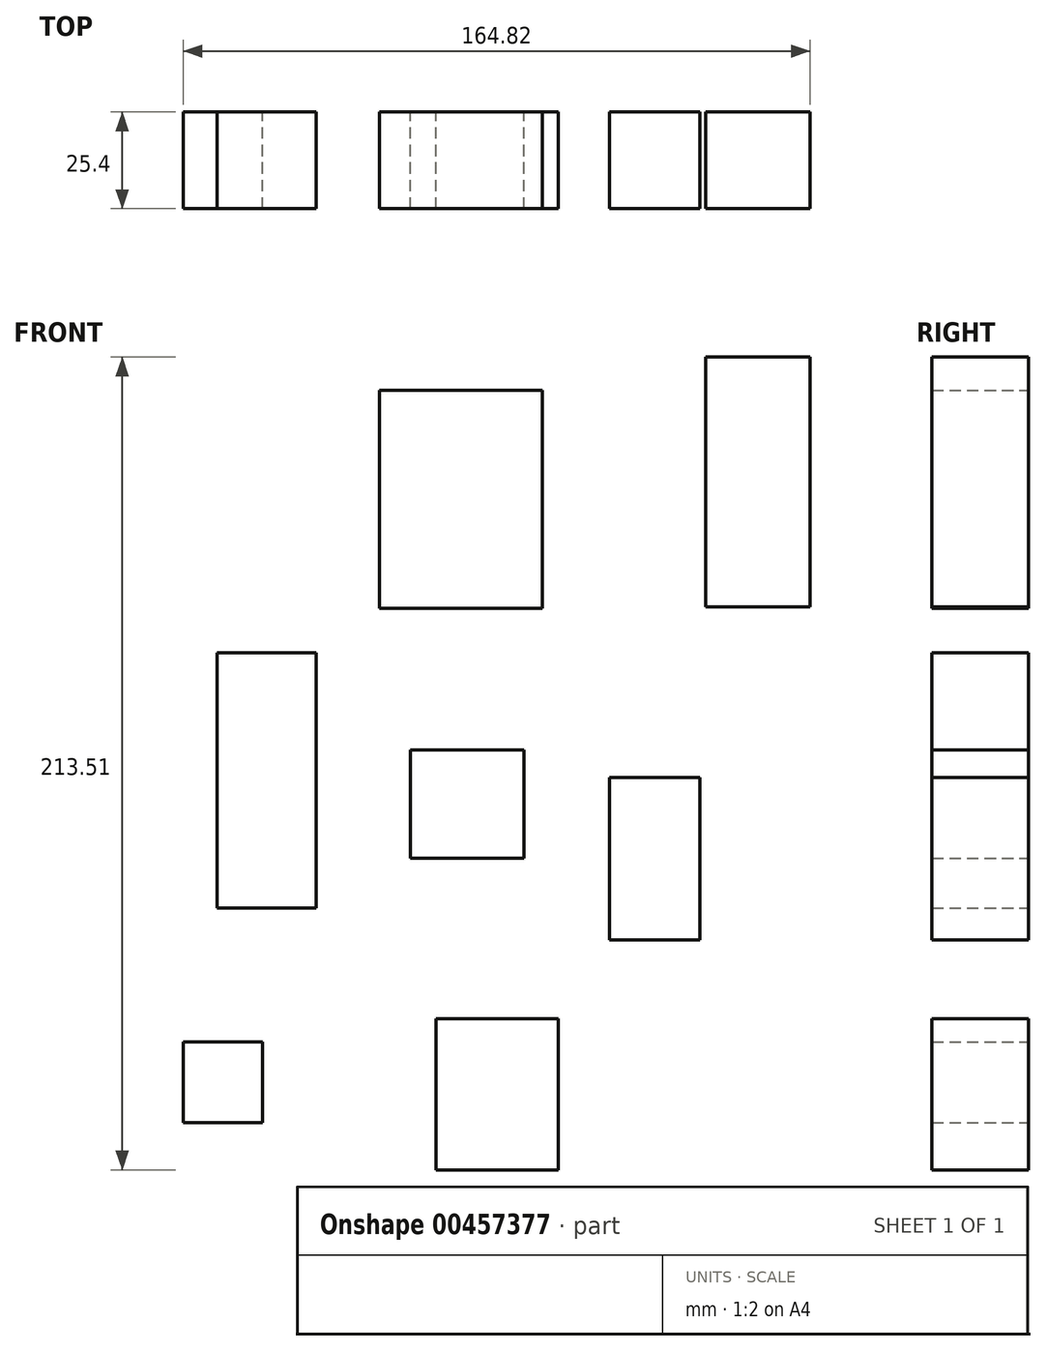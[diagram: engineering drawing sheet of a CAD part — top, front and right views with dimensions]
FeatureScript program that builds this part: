
annotation { "Feature Type Name" : "Feature", "Feature Type Description" : "" }
export const myFeature = defineFeature(function(context is Context, id is Id, definition is map)
    precondition{}
    {
        {
            var Q0;
            Q0=qCreatedBy(makeId("Front.planeOp"),FACE);
            var sketch = newSketch(context, id + "F0", { "sketchPlane" : qUnion([Q0])});
            skLineSegment(sketch, "E0.bottom", {"start": v(30.84, 136) * mm, "end": v(73.55, 136) * mm});
            skLineSegment(sketch, "E0.top", {"start": v(30.84, 78.74) * mm, "end": v(73.55, 78.74) * mm});
            skLineSegment(sketch, "E0.left", {"start": v(30.84, 136) * mm, "end": v(30.84, 78.74) * mm});
            skLineSegment(sketch, "E0.right", {"start": v(73.55, 136) * mm, "end": v(73.55, 78.74) * mm});
            skLineSegment(sketch, "E1.bottom", {"start": v(116.47, 144.68) * mm, "end": v(143.98, 144.68) * mm});
            skLineSegment(sketch, "E1.top", {"start": v(116.47, 79.07) * mm, "end": v(143.98, 79.07) * mm});
            skLineSegment(sketch, "E1.left", {"start": v(116.47, 144.68) * mm, "end": v(116.47, 79.07) * mm});
            skLineSegment(sketch, "E1.right", {"start": v(143.98, 144.68) * mm, "end": v(143.98, 79.07) * mm});
            skLineSegment(sketch, "E2.bottom", {"start": v(91.26, 34.26) * mm, "end": v(115.01, 34.26) * mm});
            skLineSegment(sketch, "E2.top", {"start": v(91.26, -8.47) * mm, "end": v(115.01, -8.47) * mm});
            skLineSegment(sketch, "E2.left", {"start": v(91.26, 34.26) * mm, "end": v(91.26, -8.47) * mm});
            skLineSegment(sketch, "E2.right", {"start": v(115.01, 34.26) * mm, "end": v(115.01, -8.47) * mm});
            skLineSegment(sketch, "E3.bottom", {"start": v(45.63, -29.12) * mm, "end": v(77.72, -29.12) * mm});
            skLineSegment(sketch, "E3.top", {"start": v(45.63, -68.83) * mm, "end": v(77.72, -68.83) * mm});
            skLineSegment(sketch, "E3.left", {"start": v(45.63, -29.12) * mm, "end": v(45.63, -68.83) * mm});
            skLineSegment(sketch, "E3.right", {"start": v(77.72, -29.12) * mm, "end": v(77.72, -68.83) * mm});
            skLineSegment(sketch, "E4.bottom", {"start": v(38.96, 41.46) * mm, "end": v(68.76, 41.46) * mm});
            skLineSegment(sketch, "E4.top", {"start": v(38.96, 12.97) * mm, "end": v(68.76, 12.97) * mm});
            skLineSegment(sketch, "E4.left", {"start": v(38.96, 41.46) * mm, "end": v(38.96, 12.97) * mm});
            skLineSegment(sketch, "E4.right", {"start": v(68.76, 41.46) * mm, "end": v(68.76, 12.97) * mm});
            skLineSegment(sketch, "E5.bottom", {"start": v(-11.88, 67) * mm, "end": v(14.17, 67) * mm});
            skLineSegment(sketch, "E5.top", {"start": v(-11.88, 0) * mm, "end": v(14.17, 0) * mm});
            skLineSegment(sketch, "E5.left", {"start": v(-11.88, 67) * mm, "end": v(-11.88, 0) * mm});
            skLineSegment(sketch, "E5.right", {"start": v(14.17, 67) * mm, "end": v(14.17, 0) * mm});
            skLineSegment(sketch, "E6.bottom", {"start": v(-20.84, -35.19) * mm, "end": v(0, -35.19) * mm});
            skLineSegment(sketch, "E6.top", {"start": v(-20.84, -56.48) * mm, "end": v(0, -56.48) * mm});
            skLineSegment(sketch, "E6.left", {"start": v(-20.84, -35.19) * mm, "end": v(-20.84, -56.48) * mm});
            skLineSegment(sketch, "E6.right", {"start": v(0, -35.19) * mm, "end": v(0, -56.48) * mm});
            skSolve(sketch);
        }
        {
            var Q0;
            Q0 = qSketchRegion(id + "F0", true);
            extrude(context, id + "F1", {"entities" : qUnion([Q0]), "depth" : 25.4 * mm});
        }
    });
